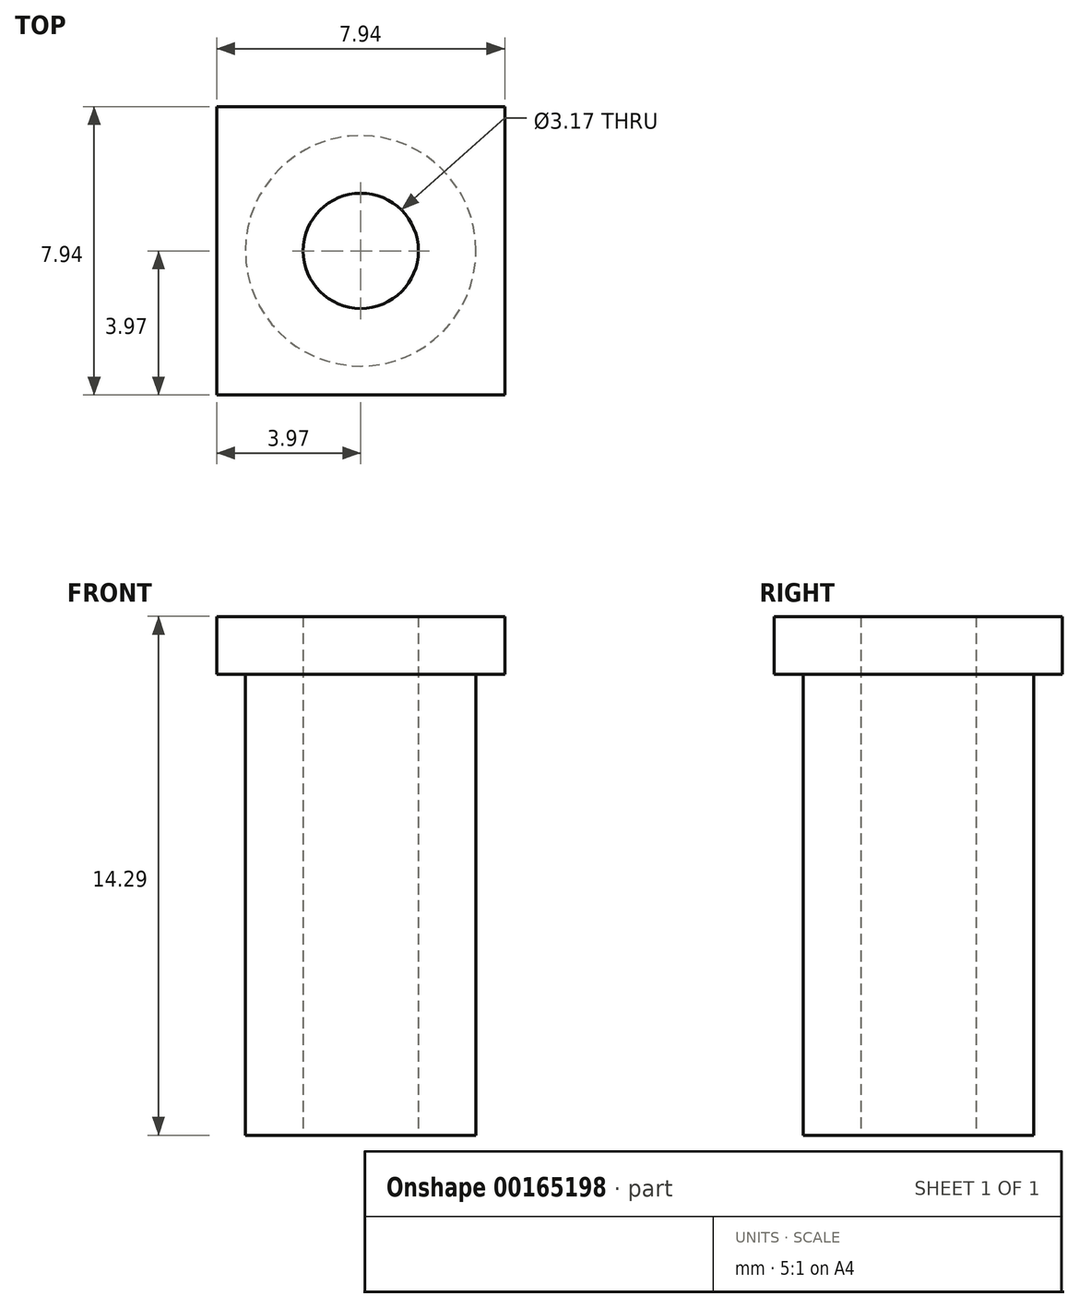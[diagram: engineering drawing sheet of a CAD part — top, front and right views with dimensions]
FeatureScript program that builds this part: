
annotation { "Feature Type Name" : "Feature", "Feature Type Description" : "" }
export const myFeature = defineFeature(function(context is Context, id is Id, definition is map)
    precondition{}
    {
        {
            var Q0;
            Q0=qCreatedBy(makeId("Top.planeOp"),FACE);
            var sketch = newSketch(context, id + "F0", { "sketchPlane" : qUnion([Q0])});
            skCircle(sketch, "E0", {"center": v(0, 0) * mm, "radius": 1.59 * mm});
            skCircle(sketch, "E1", {"center": v(0, 0) * mm, "radius": 3.18 * mm});
            skSolve(sketch);
        }
        {
            var Q0;
            Q0 = qSketchRegion(id + "F0", true);
            extrude(context, id + "F1", {"entities" : qUnion([Q0]), "depth" : 12.7 * mm});
        }
        {
            var Q0;
            Q0=makeQuery(id+"F1.opExtrude","CAP_FACE",FACE,{"disambiguationData":[OSD([sQuery(id+"F0.wireOp",EDGE,"E0"),sQuery(id+"F0.wireOp",EDGE,"E1")])],"isStart":false});
            var sketch = newSketch(context, id + "F2", { "sketchPlane" : qUnion([Q0])});
            skCircle(sketch, "E2", {"center": v(0, 0) * mm, "radius": 1.59 * mm});
            skCircle(sketch, "E3", {"center": v(0, 0) * mm, "radius": 3.97 * mm, "construction": true});
            skLineSegment(sketch, "E4.bottom", {"start": v(-3.97, -3.97) * mm, "end": v(3.97, -3.97) * mm});
            skLineSegment(sketch, "E4.top", {"start": v(-3.97, 3.97) * mm, "end": v(3.97, 3.97) * mm});
            skLineSegment(sketch, "E4.left", {"start": v(-3.97, -3.97) * mm, "end": v(-3.97, 3.97) * mm});
            skLineSegment(sketch, "E4.right", {"start": v(3.97, -3.97) * mm, "end": v(3.97, 3.97) * mm});
            skSolve(sketch);
        }
        {
            var Q0;
            Q0 = qSketchRegion(id + "F2", true);
            extrude(context, id + "F3", {"entities" : qUnion([Q0]), "operationType" : NewBodyOperationType.ADD, "depth" : 1.59 * mm});
        }
    });
